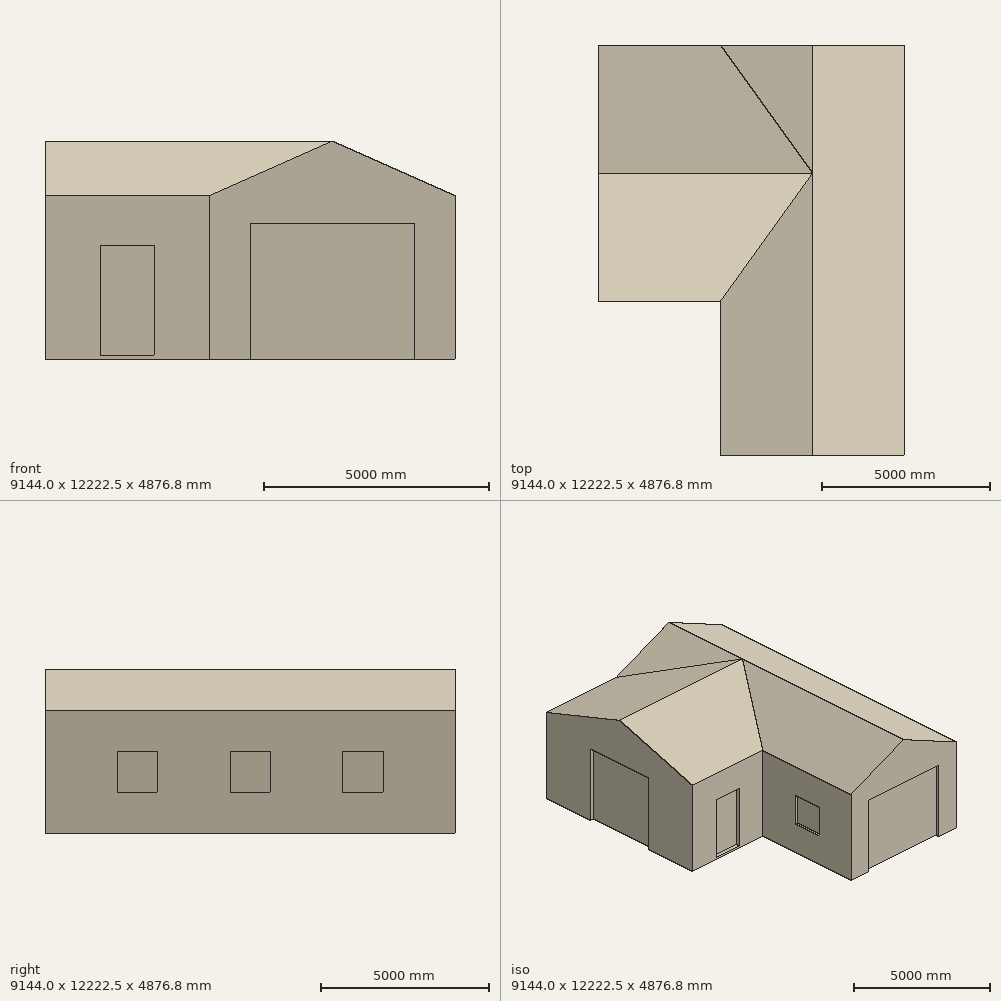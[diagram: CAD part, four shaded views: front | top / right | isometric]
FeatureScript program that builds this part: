
annotation { "Feature Type Name" : "Feature", "Feature Type Description" : "" }
export const myFeature = defineFeature(function(context is Context, id is Id, definition is map)
    precondition{}
    {
        {
            var Q0;
            Q0=qCreatedBy(makeId("Front.planeOp"),FACE);
            var sketch = newSketch(context, id + "F0", { "sketchPlane" : qUnion([Q0])});
            skLineSegment(sketch, "E0", {"start": v(0, 0) * mm, "end": v(5486.4, 0) * mm});
            skLineSegment(sketch, "E1", {"start": v(5486.4, 0) * mm, "end": v(5486.4, 3657.6) * mm});
            skLineSegment(sketch, "E2", {"start": v(5486.4, 3657.6) * mm, "end": v(2743.2, 4876.8) * mm});
            skLineSegment(sketch, "E3", {"start": v(2743.2, 4876.8) * mm, "end": v(0, 3657.6) * mm});
            skLineSegment(sketch, "E4", {"start": v(0, 3657.6) * mm, "end": v(0, 0) * mm});
            skPoint(sketch, "E5", {"position": v(2743.2, 0) * mm});
            skSolve(sketch);
        }
        {
            var Q0;
            Q0=makeQuery(id+"F0.imprint","IMPRINT",FACE,{"disambiguationData":[TD([[makeQuery(id+"F0.imprint","IMPRINT",EDGE,{"derivedFrom":sQuery(id+"F0.wireOp",EDGE,"E0")}),1.0]])]});
            extrude(context, id + "F1", {"entities" : qUnion([Q0]), "depth" : 12192 * mm, "offsetDistance" : 30.48 * mm});
        }
        {
            var Q0;
            Q0=makeQuery(id+"F1.opExtrude","SWEPT_FACE",FACE,{"disambiguationData":[OSD([sQuery(id+"F0.wireOp",EDGE,"E4")])]});
            var sketch = newSketch(context, id + "F2", { "sketchPlane" : qUnion([Q0])});
            skLineSegment(sketch, "E6", {"start": v(0, 0) * mm, "end": v(0, 3657.6) * mm});
            skLineSegment(sketch, "E7.0", {"start": v(12192, 4876.8) * mm, "end": v(0, 4876.8) * mm});
            skLineSegment(sketch, "E8.0", {"start": v(12192, 4876.8) * mm, "end": v(0, 4876.8) * mm, "construction": true});
            skLineSegment(sketch, "E9", {"start": v(0, 3657.6) * mm, "end": v(3810, 4876.8) * mm});
            skLineSegment(sketch, "E10", {"start": v(3810, 4876.8) * mm, "end": v(7620, 3657.6) * mm});
            skLineSegment(sketch, "E11", {"start": v(7620, 3657.6) * mm, "end": v(7620, 0) * mm});
            skLineSegment(sketch, "E12", {"start": v(7620, 0) * mm, "end": v(0, 0) * mm});
            skPoint(sketch, "E13", {"position": v(3810, 0) * mm});
            skSolve(sketch);
        }
        {
            var Q0;
            Q0 = qSketchRegion(id + "F2", true);
            extrude(context, id + "F3", {"entities" : qUnion([Q0]), "operationType" : NewBodyOperationType.ADD, "depth" : 3657.6 * mm, "offsetDistance" : 30.48 * mm, "hasSecondDirection" : true, "secondDirectionOppositeDirection" : true, "secondDirectionDepth" : 2743.2 * mm});
        }
        {
            var Q0;
            Q0=makeQuery(id+"F1.opExtrude","CAP_FACE",FACE,{"disambiguationData":[OSD([sQuery(id+"F0.wireOp",EDGE,"E0"),sQuery(id+"F0.wireOp",EDGE,"E1"),sQuery(id+"F0.wireOp",EDGE,"E2"),sQuery(id+"F0.wireOp",EDGE,"E3"),sQuery(id+"F0.wireOp",EDGE,"E4")])],"isStart":false});
            extrude(context, id + "F4", {"entities" : qUnion([Q0]), "operationType" : NewBodyOperationType.ADD, "depth" : 30.48 * mm, "offsetDistance" : 30.48 * mm});
        }
        {
            var Q0;
            Q0=makeQuery(id+"F4.opExtrude","CAP_FACE",FACE,{"disambiguationData":[OSD([sQuery(id+"F0.wireOp",EDGE,"E0"),sQuery(id+"F0.wireOp",EDGE,"E1"),sQuery(id+"F0.wireOp",EDGE,"E2"),sQuery(id+"F0.wireOp",EDGE,"E3"),sQuery(id+"F0.wireOp",EDGE,"E4")])],"isStart":false});
            var sketch = newSketch(context, id + "F5", { "sketchPlane" : qUnion([Q0])});
            skLineSegment(sketch, "E14.bottom", {"start": v(914.4, 0) * mm, "end": v(4572, 0) * mm});
            skLineSegment(sketch, "E14.top", {"start": v(914.4, 3048) * mm, "end": v(4572, 3048) * mm});
            skLineSegment(sketch, "E14.left", {"start": v(914.4, 0) * mm, "end": v(914.4, 3048) * mm});
            skLineSegment(sketch, "E14.right", {"start": v(4572, 0) * mm, "end": v(4572, 3048) * mm});
            skSolve(sketch);
        }
        {
            var Q0;
            Q0 = qSketchRegion(id + "F5", true);
            extrude(context, id + "F6", {"entities" : qUnion([Q0]), "operationType" : NewBodyOperationType.REMOVE, "oppositeDirection" : true, "depth" : 152.4 * mm, "offsetDistance" : 30.48 * mm});
        }
        {
            var Q0;
            Q0=makeQuery(id+"F3.opExtrude","CAP_FACE",FACE,{"disambiguationData":[OSD([sQuery(id+"F2.wireOp",EDGE,"E6"),sQuery(id+"F2.wireOp",EDGE,"E9"),sQuery(id+"F2.wireOp",EDGE,"E10"),sQuery(id+"F2.wireOp",EDGE,"E11"),sQuery(id+"F2.wireOp",EDGE,"E12")])],"isStart":false});
            var sketch = newSketch(context, id + "F7", { "sketchPlane" : qUnion([Q0])});
            skLineSegment(sketch, "E15.bottom", {"start": v(2286, 0) * mm, "end": v(5334, 0) * mm});
            skLineSegment(sketch, "E15.top", {"start": v(2286, 3048) * mm, "end": v(5334, 3048) * mm});
            skLineSegment(sketch, "E15.left", {"start": v(2286, 0) * mm, "end": v(2286, 3048) * mm});
            skLineSegment(sketch, "E15.right", {"start": v(5334, 0) * mm, "end": v(5334, 3048) * mm});
            skSolve(sketch);
        }
        {
            var Q0;
            Q0 = qSketchRegion(id + "F7", true);
            extrude(context, id + "F8", {"entities" : qUnion([Q0]), "operationType" : NewBodyOperationType.REMOVE, "oppositeDirection" : true, "depth" : 152.4 * mm, "offsetDistance" : 30.48 * mm});
        }
        {
            var Q0;
            Q0=makeQuery(id+"F3.opExtrude","SWEPT_FACE",FACE,{"disambiguationData":[OSD([sQuery(id+"F2.wireOp",EDGE,"E11")])]});
            var sketch = newSketch(context, id + "F9", { "sketchPlane" : qUnion([Q0])});
            skLineSegment(sketch, "E16.bottom", {"start": v(-2438.4, 100.58) * mm, "end": v(-1219.2, 100.58) * mm});
            skLineSegment(sketch, "E16.top", {"start": v(-2438.4, 2538.98) * mm, "end": v(-1219.2, 2538.98) * mm});
            skLineSegment(sketch, "E16.left", {"start": v(-2438.4, 100.58) * mm, "end": v(-2438.4, 2538.98) * mm});
            skLineSegment(sketch, "E16.right", {"start": v(-1219.2, 100.58) * mm, "end": v(-1219.2, 2538.98) * mm});
            skSolve(sketch);
        }
        {
            var Q0;
            Q0 = qSketchRegion(id + "F9", true);
            extrude(context, id + "F10", {"entities" : qUnion([Q0]), "operationType" : NewBodyOperationType.REMOVE, "oppositeDirection" : true, "depth" : 152.4 * mm, "offsetDistance" : 30.48 * mm});
        }
        {
            var Q0;
            {var subQ0=sQuery(id+"F0.wireOp",EDGE,"E1");Q0=makeQuery(id+"F4.boolean.opBoolean","MERGE",FACE,{"derivedFrom":[makeQuery(id+"F1.opExtrude","SWEPT_FACE",FACE,{"disambiguationData":[OSD([subQ0])]}),makeQuery(id+"F4.opExtrude","SWEPT_FACE",FACE,{"disambiguationData":[OSD([subQ0])]})]});}
            var sketch = newSketch(context, id + "F11", { "sketchPlane" : qUnion([Q0])});
            skLineSegment(sketch, "E17.bottom", {"start": v(-10088.88, 2438.4) * mm, "end": v(-8869.68, 2438.4) * mm});
            skLineSegment(sketch, "E17.top", {"start": v(-10088.88, 1219.2) * mm, "end": v(-8869.68, 1219.2) * mm});
            skLineSegment(sketch, "E17.left", {"start": v(-10088.88, 2438.4) * mm, "end": v(-10088.88, 1219.2) * mm});
            skLineSegment(sketch, "E17.right", {"start": v(-8869.68, 2438.4) * mm, "end": v(-8869.68, 1219.2) * mm});
            skLineSegment(sketch, "E18.bottom", {"start": v(-6720.84, 2438.4) * mm, "end": v(-5501.64, 2438.4) * mm});
            skLineSegment(sketch, "E18.top", {"start": v(-6720.84, 1219.2) * mm, "end": v(-5501.64, 1219.2) * mm});
            skLineSegment(sketch, "E18.left", {"start": v(-6720.84, 2438.4) * mm, "end": v(-6720.84, 1219.2) * mm});
            skLineSegment(sketch, "E18.right", {"start": v(-5501.64, 2438.4) * mm, "end": v(-5501.64, 1219.2) * mm});
            skLineSegment(sketch, "E19.bottom", {"start": v(-3368.04, 2438.4) * mm, "end": v(-2148.84, 2438.4) * mm});
            skLineSegment(sketch, "E19.top", {"start": v(-3368.04, 1219.2) * mm, "end": v(-2148.84, 1219.2) * mm});
            skLineSegment(sketch, "E19.left", {"start": v(-3368.04, 2438.4) * mm, "end": v(-3368.04, 1219.2) * mm});
            skLineSegment(sketch, "E19.right", {"start": v(-2148.84, 2438.4) * mm, "end": v(-2148.84, 1219.2) * mm});
            skPoint(sketch, "E20", {"position": v(-6111.24, 2438.4) * mm});
            skPoint(sketch, "E21", {"position": v(-6111.24, 3657.6) * mm});
            skSolve(sketch);
        }
        {
            var Q0;
            Q0 = qSketchRegion(id + "F11", true);
            extrude(context, id + "F12", {"entities" : qUnion([Q0]), "operationType" : NewBodyOperationType.REMOVE, "oppositeDirection" : true, "depth" : 100.58 * mm, "offsetDistance" : 30.48 * mm});
        }
        {
            var Q0;
            Q0=makeQuery(id+"F3.boolean.opBoolean","MERGE",FACE,{"derivedFrom":[makeQuery(id+"F1.opExtrude","CAP_FACE",FACE,{"disambiguationData":[OSD([sQuery(id+"F0.wireOp",EDGE,"E0"),sQuery(id+"F0.wireOp",EDGE,"E1"),sQuery(id+"F0.wireOp",EDGE,"E2"),sQuery(id+"F0.wireOp",EDGE,"E3"),sQuery(id+"F0.wireOp",EDGE,"E4")])],"isStart":true}),makeQuery(id+"F3.opExtrude","SWEPT_FACE",FACE,{"disambiguationData":[OSD([sQuery(id+"F2.wireOp",EDGE,"E6")])]})]});
            var sketch = newSketch(context, id + "F13", { "sketchPlane" : qUnion([Q0])});
            skLineSegment(sketch, "E22.bottom", {"start": v(-3352.8, 2438.4) * mm, "end": v(-2133.6, 2438.4) * mm});
            skLineSegment(sketch, "E22.top", {"start": v(-3352.8, 1219.2) * mm, "end": v(-2133.6, 1219.2) * mm});
            skLineSegment(sketch, "E22.left", {"start": v(-3352.8, 2438.4) * mm, "end": v(-3352.8, 1219.2) * mm});
            skLineSegment(sketch, "E22.right", {"start": v(-2133.6, 2438.4) * mm, "end": v(-2133.6, 1219.2) * mm});
            skLineSegment(sketch, "E23.bottom", {"start": v(914.4, 2438.4) * mm, "end": v(2133.6, 2438.4) * mm});
            skLineSegment(sketch, "E23.top", {"start": v(914.4, 1219.2) * mm, "end": v(2133.6, 1219.2) * mm});
            skLineSegment(sketch, "E23.left", {"start": v(914.4, 2438.4) * mm, "end": v(914.4, 1219.2) * mm});
            skLineSegment(sketch, "E23.right", {"start": v(2133.6, 2438.4) * mm, "end": v(2133.6, 1219.2) * mm});
            skPoint(sketch, "E24", {"position": v(-2743.2, 2438.4) * mm});
            skPoint(sketch, "E25", {"position": v(-2743.2, 4876.8) * mm});
            skSolve(sketch);
        }
        {
            var Q0;
            Q0 = qSketchRegion(id + "F13", true);
            extrude(context, id + "F14", {"entities" : qUnion([Q0]), "operationType" : NewBodyOperationType.REMOVE, "oppositeDirection" : true, "depth" : 100.58 * mm, "offsetDistance" : 30.48 * mm});
        }
        {
            var Q0;
            {var subQ0=sQuery(id+"F0.wireOp",EDGE,"E4");Q0=makeQuery(id+"F4.boolean.opBoolean","MERGE",FACE,{"derivedFrom":[makeQuery(id+"F1.opExtrude","SWEPT_FACE",FACE,{"disambiguationData":[OSD([subQ0])]}),makeQuery(id+"F4.opExtrude","SWEPT_FACE",FACE,{"disambiguationData":[OSD([subQ0])]})]});}
            var sketch = newSketch(context, id + "F15", { "sketchPlane" : qUnion([Q0])});
            skLineSegment(sketch, "E26.bottom", {"start": v(9326.88, 2438.4) * mm, "end": v(10546.08, 2438.4) * mm});
            skLineSegment(sketch, "E26.top", {"start": v(9326.88, 1219.2) * mm, "end": v(10546.08, 1219.2) * mm});
            skLineSegment(sketch, "E26.left", {"start": v(9326.88, 2438.4) * mm, "end": v(9326.88, 1219.2) * mm});
            skLineSegment(sketch, "E26.right", {"start": v(10546.08, 2438.4) * mm, "end": v(10546.08, 1219.2) * mm});
            skSolve(sketch);
        }
        {
            var Q0;
            Q0 = qSketchRegion(id + "F15", true);
            extrude(context, id + "F16", {"entities" : qUnion([Q0]), "operationType" : NewBodyOperationType.REMOVE, "oppositeDirection" : true, "depth" : 100.58 * mm, "offsetDistance" : 30.48 * mm});
        }
    });
